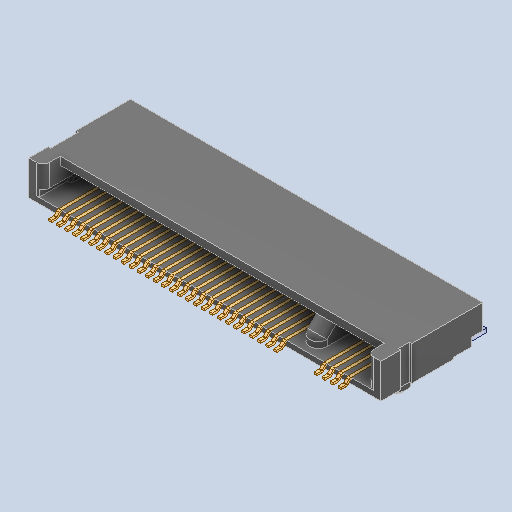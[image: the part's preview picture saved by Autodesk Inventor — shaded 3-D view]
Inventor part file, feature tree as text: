
AUTODESK INVENTOR PART (.ipt)
format: ipt  version: 2024.2 (Build 282272000, 272)  size: 1,395,712 bytes
history: native  units: in
note: dims shown in document units (in); Inventor stores cm internally (conversion verified against a paired STEP export)
features: other x71, sketch x32, mirror x1
ambient origin geometry x8: Origin, YZ Plane, XZ Plane, XY Plane, X Axis, Y Axis, Z Axis, Center Point
bodies: Solid1 (feature_tree), Solid2 (feature_tree), Solid3 (feature_tree), Solid4 (feature_tree), Solid5 (feature_tree), Solid6 (feature_tree), Solid7 (feature_tree), Solid8 (feature_tree), Solid9 (feature_tree), Solid10 (feature_tree), Solid11 (feature_tree), Solid12 (feature_tree), Solid13 (feature_tree), Solid14 (feature_tree), Solid15 (feature_tree), Solid16 (feature_tree), Solid17 (feature_tree), Solid18 (feature_tree), Solid19 (feature_tree), Solid20 (feature_tree), Solid21 (feature_tree), Solid22 (feature_tree), Solid23 (feature_tree), Solid24 (feature_tree), Solid25 (feature_tree), Solid26 (feature_tree), Solid27 (feature_tree), Solid28 (feature_tree), Solid29 (feature_tree), Solid30 (feature_tree), Solid31 (feature_tree), Solid32 (feature_tree), Solid33 (feature_tree), Solid34 (feature_tree), Solid35 (feature_tree), Solid36 (feature_tree), Solid37 (feature_tree), Solid38 (feature_tree), Solid39 (feature_tree), Solid40 (feature_tree), Solid41 (feature_tree), Solid42 (feature_tree), Solid43 (feature_tree), Solid44 (feature_tree), Solid45 (feature_tree), Solid46 (feature_tree), Solid47 (feature_tree), Solid48 (feature_tree), Solid49 (feature_tree), Solid50 (feature_tree), Solid51 (feature_tree), Solid52 (feature_tree), Solid53 (feature_tree), Solid54 (feature_tree), Solid55 (feature_tree), Solid56 (feature_tree), Solid57 (feature_tree), Solid58 (feature_tree), Solid59 (feature_tree), Solid60 (feature_tree), Solid61 (feature_tree), Solid62 (feature_tree), Solid63 (feature_tree), Solid64 (feature_tree), Solid65 (feature_tree), Solid66 (feature_tree), Solid67 (feature_tree), Solid68 (feature_tree), Solid69 (feature_tree), Solid70 (feature_tree), Solid71 (feature_tree), Solid72 (feature_tree), Solid73 (feature_tree), Solid74 (feature_tree), Solid75 (feature_tree), Solid76 (feature_tree), Solid77 (feature_tree), Solid78 (feature_tree), Solid79 (feature_tree), Solid80 (feature_tree), Solid81 (feature_tree), Solid82 (feature_tree), Solid83 (feature_tree), Solid84 (feature_tree), Solid85 (feature_tree), Solid86 (feature_tree), Solid87 (feature_tree), Solid88 (feature_tree), Solid89 (feature_tree), Solid90 (feature_tree), Solid91 (feature_tree), Solid92 (feature_tree), Solid93 (feature_tree), Solid94 (feature_tree), Solid95 (feature_tree), Solid96 (feature_tree), Solid97 (feature_tree), Solid98 (feature_tree), Solid99 (feature_tree), Solid100 (feature_tree), Solid101 (feature_tree), Solid102 (feature_tree), Solid103 (feature_tree), Solid104 (feature_tree)
feature tree (104):
  other  "Housing"
  other  "Pin 2"
  sketch  "Sketch-Pattern1[1]"
  sketch  "Sketch-Pattern1[2]"
  sketch  "Sketch-Pattern1[3]"
  sketch  "Sketch-Pattern1[4]"
  sketch  "Sketch-Pattern1[5]"
  sketch  "Sketch-Pattern1[6]"
  sketch  "Sketch-Pattern1[7]"
  sketch  "Sketch-Pattern1[8]"
  sketch  "Sketch-Pattern1[9]"
  sketch  "Sketch-Pattern1[10]"
  sketch  "Sketch-Pattern1[11]"
  sketch  "Sketch-Pattern1[12]"
  sketch  "Sketch-Pattern1[13]"
  sketch  "Sketch-Pattern1[14]"
  sketch  "Sketch-Pattern1[15]"
  sketch  "Sketch-Pattern1[16]"
  sketch  "Sketch-Pattern1[17]"
  sketch  "Sketch-Pattern1[18]"
  sketch  "Sketch-Pattern1[19]"
  sketch  "Sketch-Pattern1[20]"
  sketch  "Sketch-Pattern1[21]"
  sketch  "Sketch-Pattern1[22]"
  sketch  "Sketch-Pattern1[23]"
  sketch  "Sketch-Pattern1[24]"
  sketch  "Sketch-Pattern1[25]"
  sketch  "Sketch-Pattern1[26]"
  sketch  "Sketch-Pattern1[27]"
  sketch  "Sketch-Pattern1[28]"
  sketch  "Sketch-Pattern1[29]"
  sketch  "Sketch-Pattern1[30]"
  sketch  "Sketch-Pattern1[31]"
  sketch  "Sketch-Pattern1[32]"
  other  "Pin 1"
  other  "LPattern3[1]"
  other  "LPattern3[2]"
  other  "LPattern3[3]"
  other  "LPattern3[4]"
  other  "LPattern3[5]"
  other  "LPattern3[6]"
  other  "LPattern3[7]"
  other  "LPattern3[8]"
  other  "LPattern3[9]"
  other  "LPattern3[10]"
  other  "LPattern3[11]"
  other  "LPattern3[12]"
  other  "LPattern3[13]"
  other  "LPattern3[14]"
  other  "LPattern3[15]"
  other  "LPattern3[16]"
  other  "LPattern3[17]"
  other  "LPattern3[18]"
  other  "LPattern3[19]"
  other  "LPattern3[20]"
  other  "LPattern3[21]"
  other  "LPattern3[22]"
  other  "LPattern3[23]"
  other  "LPattern3[24]"
  other  "LPattern3[25]"
  other  "LPattern3[26]"
  other  "LPattern3[27]"
  other  "LPattern3[28]"
  other  "Boss-Extrude8[1]"
  other  "LPattern4[1]"
  other  "LPattern4[2]"
  other  "LPattern4[3]"
  other  "LPattern4[4]"
  other  "Boss-Extrude8[2]"
  other  "LPattern4[5]"
  other  "LPattern4[6]"
  other  "LPattern4[7]"
  other  "LPattern4[8]"
  other  "Contact 1"
  other  "LPattern3[29]"
  other  "LPattern3[30]"
  other  "LPattern3[31]"
  other  "LPattern3[32]"
  other  "LPattern3[33]"
  other  "LPattern3[34]"
  other  "LPattern3[35]"
  other  "LPattern3[36]"
  other  "LPattern3[37]"
  other  "LPattern3[38]"
  other  "LPattern3[39]"
  other  "LPattern3[40]"
  other  "LPattern3[41]"
  other  "LPattern3[42]"
  other  "LPattern3[43]"
  other  "LPattern3[44]"
  other  "LPattern3[45]"
  other  "LPattern3[46]"
  other  "LPattern3[47]"
  other  "LPattern3[48]"
  other  "LPattern3[49]"
  other  "LPattern3[50]"
  other  "LPattern3[51]"
  other  "LPattern3[52]"
  other  "LPattern3[53]"
  other  "LPattern3[54]"
  other  "LPattern3[55]"
  other  "LPattern3[56]"
  other  "Boss-Extrude9"
  mirror  "Mirror1"
